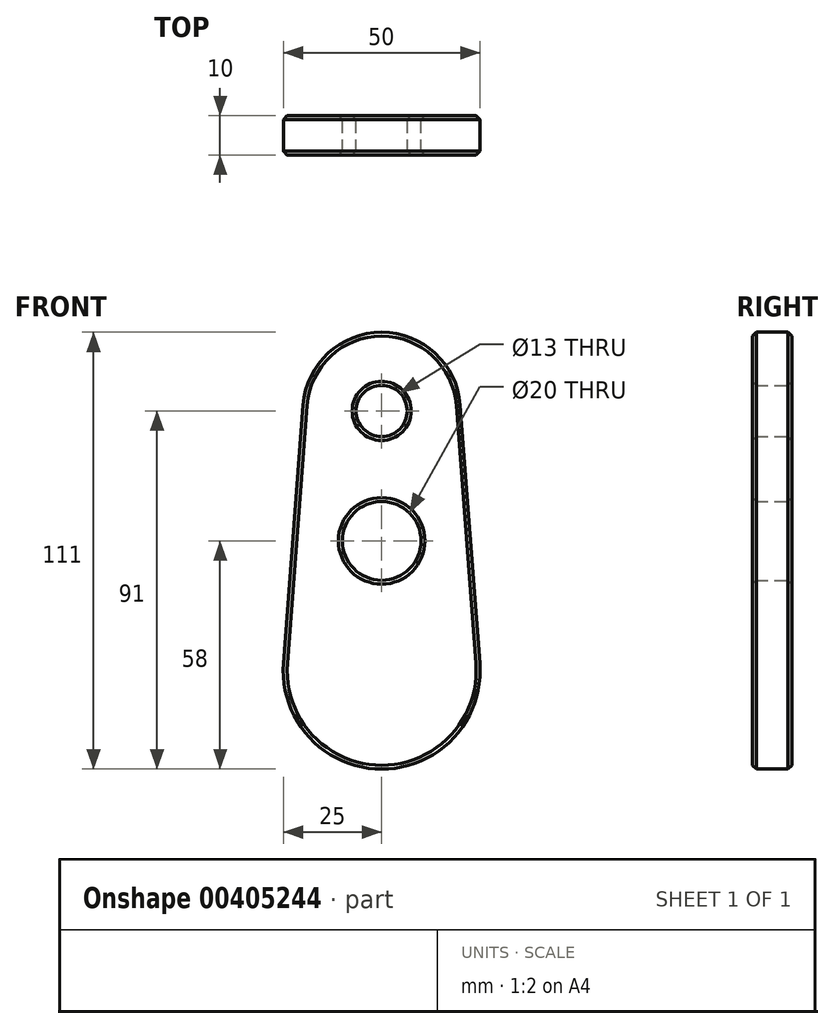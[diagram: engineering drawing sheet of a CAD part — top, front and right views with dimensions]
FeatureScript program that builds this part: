
annotation { "Feature Type Name" : "Feature", "Feature Type Description" : "" }
export const myFeature = defineFeature(function(context is Context, id is Id, definition is map)
    precondition{}
    {
        {
            var Q0;
            Q0=qCreatedBy(makeId("Front.planeOp"),FACE);
            var sketch = newSketch(context, id + "F0", { "sketchPlane" : qUnion([Q0])});
            skCircle(sketch, "E0", {"center": v(0, 0) * mm, "radius": 6.5 * mm});
            skCircle(sketch, "E1", {"center": v(0, -33) * mm, "radius": 10 * mm});
            skArc(sketch, "E2", {"start": v(-24.93, -64.1) * mm, "mid": v(0, -91) * mm, "end": v(24.93, -64.1) * mm});
            skArc(sketch, "E3", {"start": v(-19.94, 1.52) * mm, "mid": v(0, 20) * mm, "end": v(19.94, 1.52) * mm});
            skLineSegment(sketch, "E4", {"start": v(-24.93, -64.1) * mm, "end": v(-19.94, 1.52) * mm});
            skLineSegment(sketch, "E5", {"start": v(19.94, 1.52) * mm, "end": v(24.93, -64.1) * mm});
            skSolve(sketch);
        }
        {
            var Q0;
            Q0=makeQuery(id+"F0.imprint","IMPRINT",FACE,{"disambiguationData":[TD([[makeQuery(id+"F0.imprint","IMPRINT",EDGE,{"derivedFrom":sQuery(id+"F0.wireOp",EDGE,"E0")}),-1.0]])]});
            extrude(context, id + "F1", {"entities" : qUnion([Q0]), "endBound" : BoundingType.SYMMETRIC, "depth" : 10 * mm});
        }
        {
            var Q0;
            Q0=makeQuery(id+"F1.opExtrude","CAP_FACE",FACE,{"disambiguationData":[OSD([sQuery(id+"F0.wireOp",EDGE,"E0"),sQuery(id+"F0.wireOp",EDGE,"E1"),sQuery(id+"F0.wireOp",EDGE,"E2"),sQuery(id+"F0.wireOp",EDGE,"E3"),sQuery(id+"F0.wireOp",EDGE,"E4"),sQuery(id+"F0.wireOp",EDGE,"E5")])],"isStart":false});
            chamfer(context, id + "F2", {"entities" : qUnion([Q0]), "chamferType" : ChamferType.OFFSET_ANGLE, "width" : 1 * mm, "oppositeDirection" : false, "angle" : 45 * degree, "tangentPropagation" : true});
        }
        {
            var Q0;
            Q0=makeQuery(id+"F1.opExtrude","CAP_FACE",FACE,{"disambiguationData":[OSD([sQuery(id+"F0.wireOp",EDGE,"E0"),sQuery(id+"F0.wireOp",EDGE,"E1"),sQuery(id+"F0.wireOp",EDGE,"E2"),sQuery(id+"F0.wireOp",EDGE,"E3"),sQuery(id+"F0.wireOp",EDGE,"E4"),sQuery(id+"F0.wireOp",EDGE,"E5")])],"isStart":true});
            chamfer(context, id + "F3", {"entities" : qUnion([Q0]), "chamferType" : ChamferType.OFFSET_ANGLE, "width" : 1 * mm, "oppositeDirection" : false, "angle" : 45 * degree, "tangentPropagation" : true});
        }
    });
